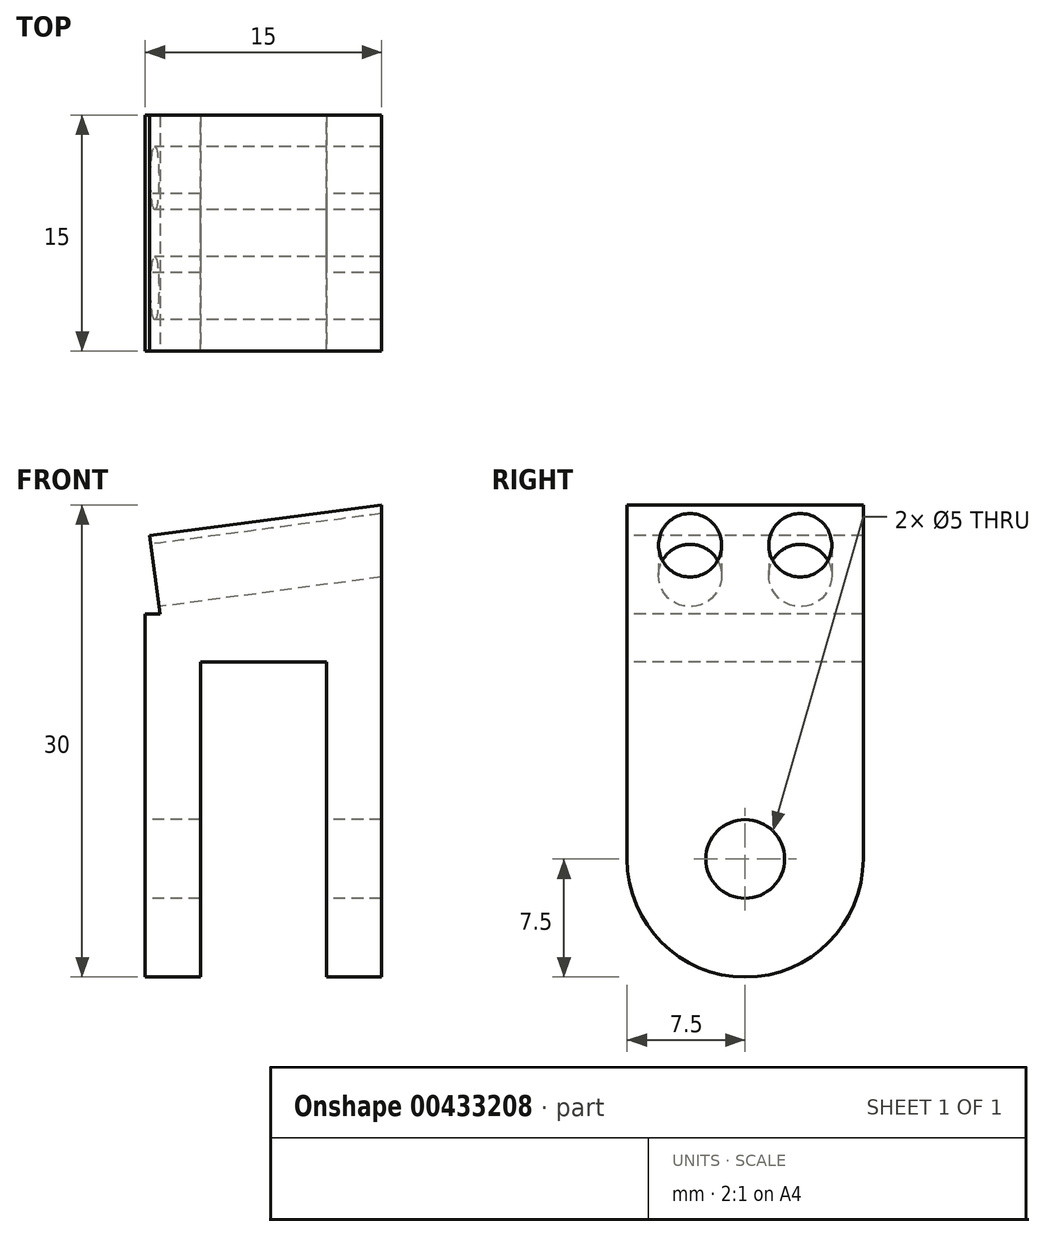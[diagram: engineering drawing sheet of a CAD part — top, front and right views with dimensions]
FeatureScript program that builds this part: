
annotation { "Feature Type Name" : "Feature", "Feature Type Description" : "" }
export const myFeature = defineFeature(function(context is Context, id is Id, definition is map)
    precondition{}
    {
        {
            var Q0;
            Q0=qCreatedBy(makeId("Front.planeOp"),FACE);
            var sketch = newSketch(context, id + "F0", { "sketchPlane" : qUnion([Q0])});
            skLineSegment(sketch, "E0.bottom", {"start": v(7.5, 15) * mm, "end": v(-7.5, 15) * mm});
            skLineSegment(sketch, "E0.top", {"start": v(7.5, -15) * mm, "end": v(-7.5, -15) * mm});
            skLineSegment(sketch, "E0.left", {"start": v(7.5, 15) * mm, "end": v(7.5, -15) * mm});
            skLineSegment(sketch, "E0.right", {"start": v(-7.5, 15) * mm, "end": v(-7.5, -15) * mm});
            skPoint(sketch, "E0.middle", {"position": v(0, 0) * mm});
            skSolve(sketch);
        }
        {
            var Q0;
            Q0 = qSketchRegion(id + "F0", true);
            extrude(context, id + "F1", {"entities" : qUnion([Q0]), "depth" : 15 * mm});
        }
        {
            var Q0;
            Q0=makeQuery(id+"F1.opExtrude","CAP_FACE",FACE,{"disambiguationData":[OSD([sQuery(id+"F0.wireOp",EDGE,"E0.bottom"),sQuery(id+"F0.wireOp",EDGE,"E0.top"),sQuery(id+"F0.wireOp",EDGE,"E0.left"),sQuery(id+"F0.wireOp",EDGE,"E0.right")])],"isStart":false});
            var sketch = newSketch(context, id + "F2", { "sketchPlane" : qUnion([Q0])});
            skLineSegment(sketch, "E1.bottom", {"start": v(-4, -15) * mm, "end": v(4, -15) * mm});
            skLineSegment(sketch, "E1.top", {"start": v(-4, 5) * mm, "end": v(4, 5) * mm});
            skLineSegment(sketch, "E1.left", {"start": v(-4, -15) * mm, "end": v(-4, 5) * mm});
            skLineSegment(sketch, "E1.right", {"start": v(4, -15) * mm, "end": v(4, 5) * mm});
            skLineSegment(sketch, "E2", {"start": v(-7.5, 13) * mm, "end": v(7.5, 15) * mm});
            skLineSegment(sketch, "E3", {"start": v(7.5, 15) * mm, "end": v(-7.5, 15) * mm});
            skLineSegment(sketch, "E4", {"start": v(-7.5, 15) * mm, "end": v(-7.5, 13) * mm});
            skLineSegment(sketch, "E5", {"start": v(-7.5, 15) * mm, "end": v(-6.57, 8.06) * mm});
            skLineSegment(sketch, "E6", {"start": v(-6.57, 8.06) * mm, "end": v(-7.5, 8.06) * mm});
            skLineSegment(sketch, "E7", {"start": v(-7.5, 8.06) * mm, "end": v(-7.5, 15) * mm});
            skSolve(sketch);
        }
        {
            var Q0;
            Q0 = qSketchRegion(id + "F2", true);
            extrude(context, id + "F3", {"entities" : qUnion([Q0]), "operationType" : NewBodyOperationType.REMOVE, "oppositeDirection" : true, "depth" : 25.4 * mm});
        }
        {
            var Q0;
            {var subQ0=sQuery(id+"F0.wireOp",EDGE,"E0.right");var subQ1=sQuery(id+"F0.wireOp",EDGE,"E0.top");Q0=makeQuery(id+"F3.boolean.opBoolean","SPLIT",EDGE,{"disambiguationData":[TD([makeQuery(id+"F1.opExtrude","SWEPT_FACE",FACE,{"disambiguationData":[OSD([subQ0])]})])],"derivedFrom":makeQuery(id+"F1.opExtrude","CAP_EDGE",EDGE,{"disambiguationData":[OSD([subQ1])],"isStart":false})});}
            var Q1;
            {var subQ0=sQuery(id+"F0.wireOp",EDGE,"E0.right");var subQ1=sQuery(id+"F0.wireOp",EDGE,"E0.top");Q1=makeQuery(id+"F3.boolean.opBoolean","SPLIT",EDGE,{"disambiguationData":[TD([makeQuery(id+"F1.opExtrude","SWEPT_FACE",FACE,{"disambiguationData":[OSD([subQ0])]})])],"derivedFrom":makeQuery(id+"F1.opExtrude","CAP_EDGE",EDGE,{"disambiguationData":[OSD([subQ1])],"isStart":true})});}
            var Q2;
            {var subQ0=sQuery(id+"F0.wireOp",EDGE,"E0.left");var subQ1=sQuery(id+"F0.wireOp",EDGE,"E0.top");Q2=makeQuery(id+"F3.boolean.opBoolean","SPLIT",EDGE,{"disambiguationData":[TD([makeQuery(id+"F1.opExtrude","SWEPT_FACE",FACE,{"disambiguationData":[OSD([subQ0])]})])],"derivedFrom":makeQuery(id+"F1.opExtrude","CAP_EDGE",EDGE,{"disambiguationData":[OSD([subQ1])],"isStart":true})});}
            var Q3;
            {var subQ0=sQuery(id+"F0.wireOp",EDGE,"E0.left");var subQ1=sQuery(id+"F0.wireOp",EDGE,"E0.top");Q3=makeQuery(id+"F3.boolean.opBoolean","SPLIT",EDGE,{"disambiguationData":[TD([makeQuery(id+"F1.opExtrude","SWEPT_FACE",FACE,{"disambiguationData":[OSD([subQ0])]})])],"derivedFrom":makeQuery(id+"F1.opExtrude","CAP_EDGE",EDGE,{"disambiguationData":[OSD([subQ1])],"isStart":false})});}
            fillet(context, id + "F4", {"entities" : qUnion([Q0, Q1, Q2, Q3]), "radius" : 7.5 * mm, "tangentPropagation" : true, "allowEdgeOverflow" : false});
        }
        {
            var Q0;
            Q0=makeQuery(id+"F3.boolean.opBoolean","COPY",FACE,{"derivedFrom":makeQuery(id+"F3.opExtrude","SWEPT_FACE",FACE,{"disambiguationData":[OSD([sQuery(id+"F2.wireOp",EDGE,"E5")])]})});
            var sketch = newSketch(context, id + "F5", { "sketchPlane" : qUnion([Q0])});
            skCircle(sketch, "E8", {"center": v(4, 11.33) * mm, "radius": 2 * mm});
            skCircle(sketch, "E9", {"center": v(11, 11.33) * mm, "radius": 2 * mm});
            skSolve(sketch);
        }
        {
            var Q0;
            Q0 = qSketchRegion(id + "F5", true);
            extrude(context, id + "F6", {"entities" : qUnion([Q0]), "operationType" : NewBodyOperationType.REMOVE, "oppositeDirection" : true, "depth" : 25.4 * mm});
        }
        {
            var Q0;
            Q0=makeQuery(id+"F1.opExtrude","SWEPT_FACE",FACE,{"disambiguationData":[OSD([sQuery(id+"F0.wireOp",EDGE,"E0.right")])]});
            var sketch = newSketch(context, id + "F7", { "sketchPlane" : qUnion([Q0])});
            skCircle(sketch, "E10", {"center": v(7.5, -7.5) * mm, "radius": 2.5 * mm});
            skSolve(sketch);
        }
        {
            var Q0;
            Q0 = qSketchRegion(id + "F7", true);
            extrude(context, id + "F8", {"entities" : qUnion([Q0]), "operationType" : NewBodyOperationType.REMOVE, "oppositeDirection" : true, "depth" : 25.4 * mm});
        }
    });
